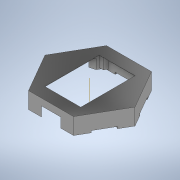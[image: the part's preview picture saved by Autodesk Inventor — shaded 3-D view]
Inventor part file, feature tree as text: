
AUTODESK INVENTOR PART (.ipt)
format: ipt  version: 2020 (Build 240168000, 168)  size: 333,824 bytes
history: native  units: mm
features: extrude x7, sketch x2, pattern_circular x1
ambient origin geometry x8: Origin, YZ Plane, XZ Plane, XY Plane, X Axis, Y Axis, Z Axis, Center Point
bodies: Body1 (feature_tree)
feature tree (10):
  sketch  "Sketch6"  dims[d44=97.0mm d72=6.5mm]
  extrude  "Fronte"  Depth=6.5mm
  extrude  "Esterno"  Depth=0.5mm TaperAngle=0.0deg
  extrude  "Strip"  Depth=15.0mm
  extrude  "Passacavi"  Depth=6.5mm
  extrude  "ScavoStrip"  Depth=30.0mm
  extrude  "ScreenDist0.8"  Depth=2.5mm
  extrude  "SupportoViti"  Depth=2.5mm
  pattern_circular  "RipetizioneSupports"  [2 undecoded]
  sketch  "Sketch7"  dims[d77=140.0mm d85=0.5mm d86=0.0mm d87=15.0mm d88=6.5mm d89=30.0mm d91=2.5mm d92=2.5mm d95=1.25mm d96=25.0mm d97=2.5mm d98=25.0mm d99=135.0deg d100=0.0mm d101=25.0mm d102=0.0mm d103=10.0mm d104=0.0mm d105=3.0mm d106=0.0mm d107=5.0mm d108=0.0mm d111=0.8mm d112=0.0mm d114=1.7mm d115=23.0mm d116=0.0mm d117=3.0mm d118=60.0mm d119=360.0deg d121=3.0mm d123=6.0mm]
note: 2 required parameter values undecoded (feature->parameter linkage not recoverable at this tier; creation-order binding heuristic only, values carry confidence <= 0.55)
